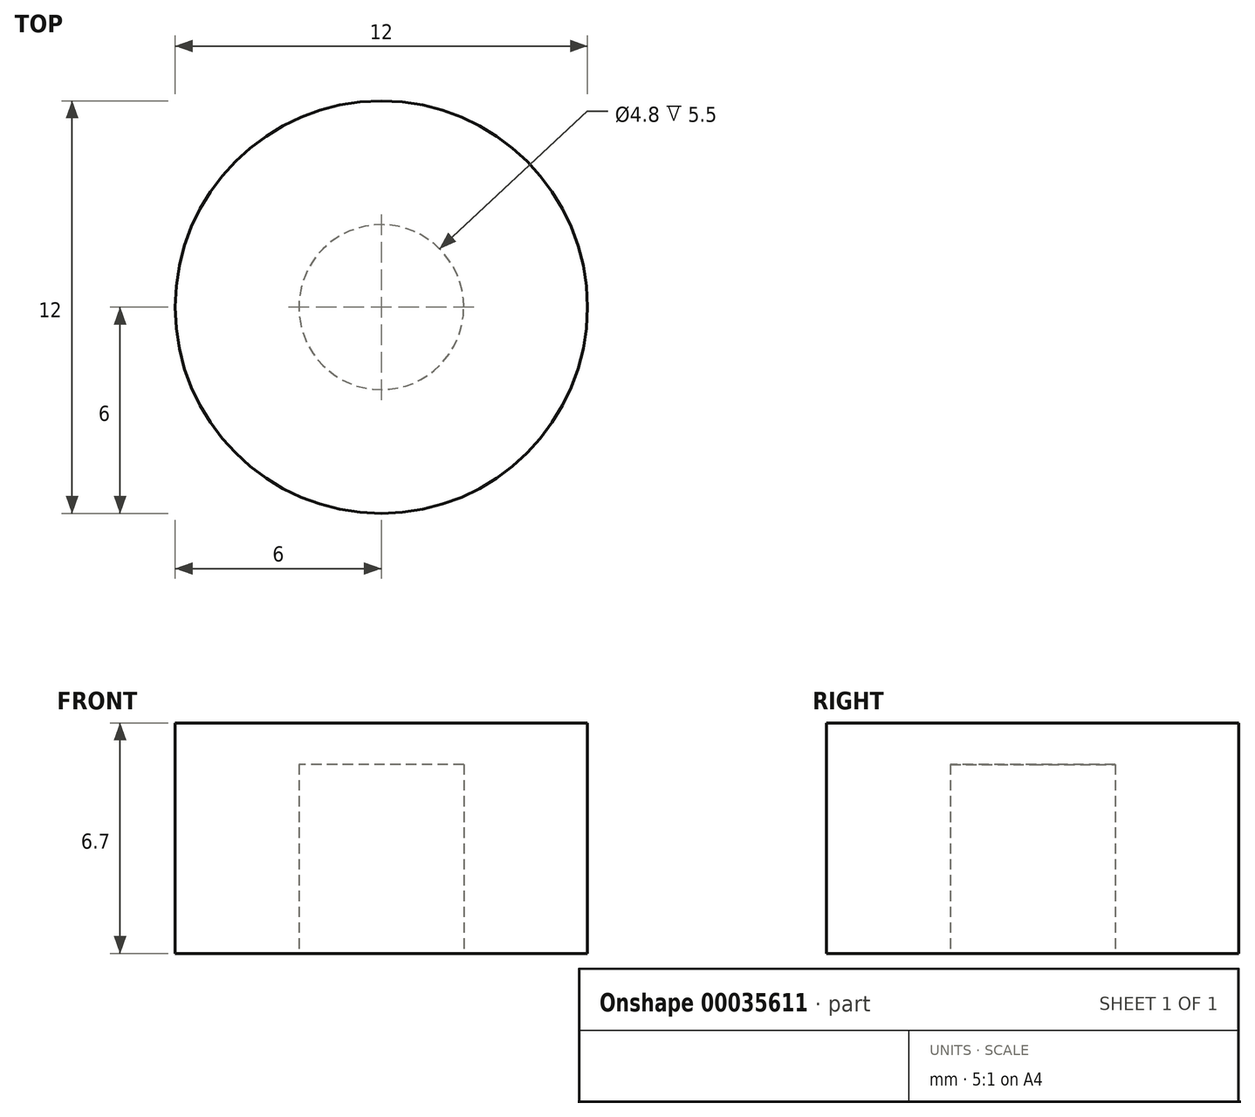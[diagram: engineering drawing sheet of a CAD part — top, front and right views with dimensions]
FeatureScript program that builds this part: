
annotation { "Feature Type Name" : "Feature", "Feature Type Description" : "" }
export const myFeature = defineFeature(function(context is Context, id is Id, definition is map)
    precondition{}
    {
        {
            var Q0;
            Q0=qCreatedBy(makeId("Top.planeOp"),FACE);
            var sketch = newSketch(context, id + "F0", { "sketchPlane" : qUnion([Q0])});
            skCircle(sketch, "E0", {"center": v(0, 0) * mm, "radius": 6 * mm});
            skCircle(sketch, "E1", {"center": v(0, 0) * mm, "radius": 2.4 * mm});
            skSolve(sketch);
        }
        {
            var Q0;
            Q0=qSketchRegion(id+"F0",true);
            extrude(context, id + "F1", {"entities" : qUnion([Q0]), "depth" : 5.5 * mm});
        }
        {
            var Q0;
            Q0=makeQuery(id+"F1.opExtrude","CAP_FACE",FACE,{"disambiguationData":[OSD([sQuery(id+"F0.wireOp",EDGE,"E0"),sQuery(id+"F0.wireOp",EDGE,"E1")])],"isStart":false});
            var sketch = newSketch(context, id + "F2", { "sketchPlane" : qUnion([Q0])});
            skCircle(sketch, "E2", {"center": v(0, 0) * mm, "radius": 6 * mm});
            skSolve(sketch);
        }
        {
            var Q0;
            Q0 = qSketchRegion(id + "F2", true);
            extrude(context, id + "F3", {"entities" : qUnion([Q0]), "operationType" : NewBodyOperationType.ADD, "depth" : 1.2 * mm});
        }
    });
